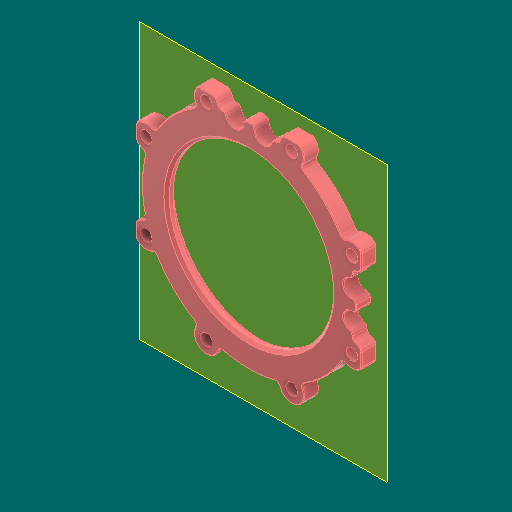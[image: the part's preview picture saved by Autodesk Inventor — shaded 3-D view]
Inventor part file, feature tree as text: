
AUTODESK INVENTOR PART (.ipt)
format: ipt  version: 2023.1 (Build 271208000, 208)  size: 353,792 bytes
history: native  units: in
note: dims shown in document units (in); Inventor stores cm internally (conversion verified against a paired STEP export)
features: other x3, sketch x2, plane x1
ambient origin geometry x8: Origin, YZ Plane, XZ Plane, XY Plane, X Axis, Y Axis, Z Axis, Center Point
bodies: Solid1 (feature_tree)
feature tree (6):
  other  "UpperRaceRing_MIR.ipt"
  other  "Solid1::UpperRaceRing_MIR.ipt"
  other  "TaggingFeature1"
  sketch  "Sketch1"  dims[d0=0.3937in]
  sketch  "Sketch2"
  plane  "Work Plane1"
